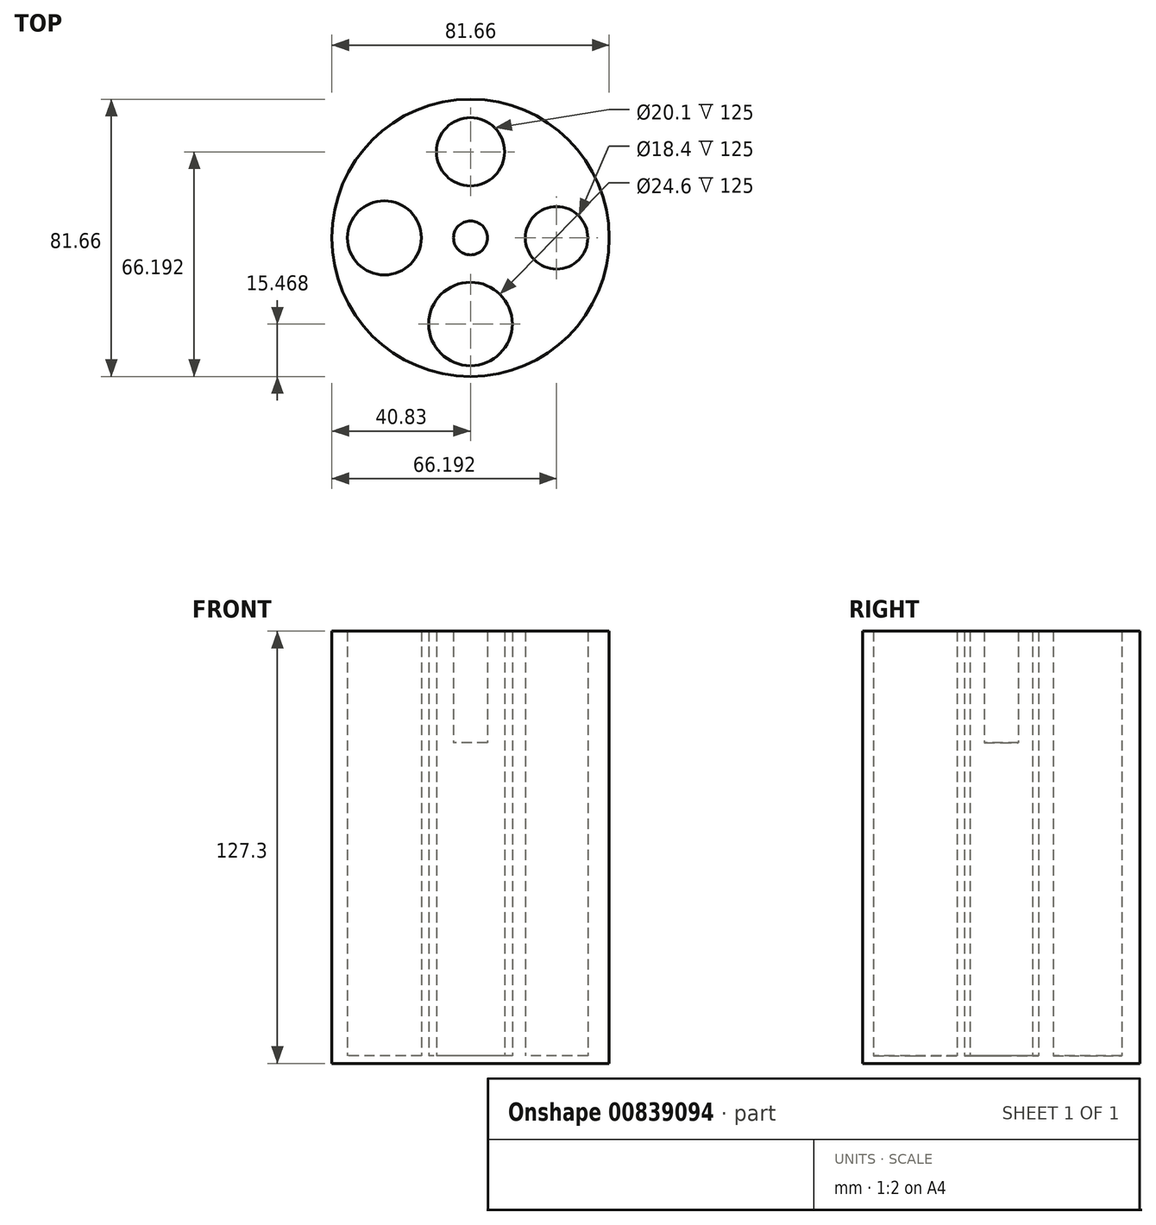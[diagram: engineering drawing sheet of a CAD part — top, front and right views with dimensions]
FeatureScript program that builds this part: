
annotation { "Feature Type Name" : "Feature", "Feature Type Description" : "" }
export const myFeature = defineFeature(function(context is Context, id is Id, definition is map)
    precondition{}
    {
        {
            var Q0;
            Q0=qCreatedBy(makeId("Top.planeOp"),FACE);
            var sketch = newSketch(context, id + "F0", { "sketchPlane" : qUnion([Q0])});
            skCircle(sketch, "E0", {"center": v(0, -25.36) * mm, "radius": 12.3 * mm});
            skCircle(sketch, "E1", {"center": v(25.36, 0) * mm, "radius": 9.2 * mm});
            skCircle(sketch, "E2", {"center": v(0, 25.36) * mm, "radius": 10.05 * mm});
            skCircle(sketch, "E3", {"center": v(-25.36, 0) * mm, "radius": 10.9 * mm});
            skCircle(sketch, "E4", {"center": v(0, 0) * mm, "radius": 40.83 * mm});
            skSolve(sketch);
        }
        {
            var Q0;
            Q0 = qSketchRegion(id + "F0", true);
            extrude(context, id + "F1", {"entities" : qUnion([Q0]), "depth" : 125 * mm, "offsetDistance" : 25 * mm});
        }
        {
            var Q0;
            Q0=qCreatedBy(makeId("Top.planeOp"),FACE);
            var sketch = newSketch(context, id + "F2", { "sketchPlane" : qUnion([Q0])});
            skCircle(sketch, "E5", {"center": v(0, 0) * mm, "radius": 40.83 * mm});
            skSolve(sketch);
        }
        {
            var Q0;
            Q0 = qSketchRegion(id + "F2", true);
            extrude(context, id + "F3", {"entities" : qUnion([Q0]), "operationType" : NewBodyOperationType.ADD, "oppositeDirection" : true, "depth" : 2.3 * mm, "offsetDistance" : 25 * mm});
        }
        {
            var Q0;
            Q0=qCreatedBy(makeId("Top.planeOp"),FACE);
            var sketch = newSketch(context, id + "F4", { "sketchPlane" : qUnion([Q0])});
            skCircle(sketch, "E6", {"center": v(0, 0) * mm, "radius": 5 * mm});
            skSolve(sketch);
        }
        {
            var Q0;
            Q0 = qSketchRegion(id + "F4", true);
            extrude(context, id + "F5", {"entities" : qUnion([Q0]), "operationType" : NewBodyOperationType.REMOVE, "depth" : 125 * mm, "offsetDistance" : 25 * mm});
        }
        {
            var Q0;
            Q0=qCreatedBy(makeId("Top.planeOp"),FACE);
            var sketch = newSketch(context, id + "F6", { "sketchPlane" : qUnion([Q0])});
            skCircle(sketch, "E7", {"center": v(0, 0) * mm, "radius": 5 * mm});
            skSolve(sketch);
        }
        {
            var Q0;
            Q0 = qSketchRegion(id + "F6", true);
            extrude(context, id + "F7", {"entities" : qUnion([Q0]), "operationType" : NewBodyOperationType.ADD, "depth" : 92.1 * mm, "offsetDistance" : 25 * mm});
        }
        {
            var Q0;
            Q0 = qSketchRegion(id + "F6", true);
            extrude(context, id + "F8", {"entities" : qUnion([Q0]), "operationType" : NewBodyOperationType.ADD, "depth" : 92.1 * mm, "offsetDistance" : 25 * mm});
        }
        {
            var Q0;
            Q0=qCreatedBy(makeId("Top.planeOp"),FACE);
            var sketch = newSketch(context, id + "F9", { "sketchPlane" : qUnion([Q0])});
            skCircle(sketch, "E8", {"center": v(0, 0) * mm, "radius": 4.09 * mm});
            skCircle(sketch, "E9", {"center": v(0, 0) * mm, "radius": 4.99 * mm});
            skCircle(sketch, "E10", {"center": v(0, 0) * mm, "radius": 40.83 * mm});
            skCircle(sketch, "E11", {"center": v(0, 0) * mm, "radius": 39.93 * mm});
            skSolve(sketch);
        }
        {
            var Q0;
            Q0=sQuery(id+"F9.wireOp",EDGE,"E8");
            var Q1;
            Q1=sQuery(id+"F9.wireOp",EDGE,"E9");
            var Q2;
            Q2=sQuery(id+"F9.wireOp",EDGE,"E11");
            var Q3;
            Q3=sQuery(id+"F9.wireOp",EDGE,"E10");
            extrude(context, id + "F10", {"bodyType" : ToolBodyType.SURFACE, "surfaceEntities" : qUnion([Q0, Q1, Q2, Q3]), "depth" : 128.3 * mm, "offsetDistance" : 25 * mm});
        }
    });
